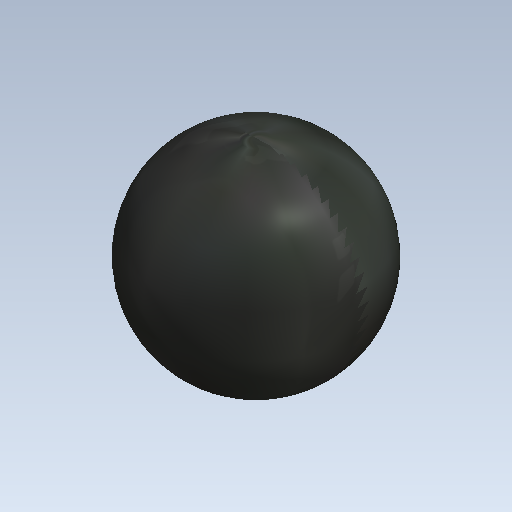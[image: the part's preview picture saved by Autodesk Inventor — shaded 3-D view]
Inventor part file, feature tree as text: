
AUTODESK INVENTOR PART (.ipt)
format: ipt  version: 2021 (Build 250183000, 183)  size: 129,536 bytes
history: native  units: mm (DEFAULTED — no unit token found)
features: other x7, revolve x1, sketch x1
ambient origin geometry x8: Origin, YZ Plane, XZ Plane, XY Plane, X Axis, Y Axis, Z Axis, Center Point
bodies: Solid1 (feature_tree)
feature tree (9):
  revolve  "Revolution1"  [1 undecoded]
  other  "ip_op_b_XY"
  other  "ip_op_b_YZ"
  other  "ip_op_b_ZX"
  other  "ip_op_b_X"
  other  "ip_op_b_Y"
  other  "ip_op_b_Z"
  other  "ip_op_b_Center"
  sketch  "Sketch_1"  dims[d0=360.0deg]
note: 1 required parameter value undecoded (feature->parameter linkage not recoverable at this tier; creation-order binding heuristic only, values carry confidence <= 0.55)
